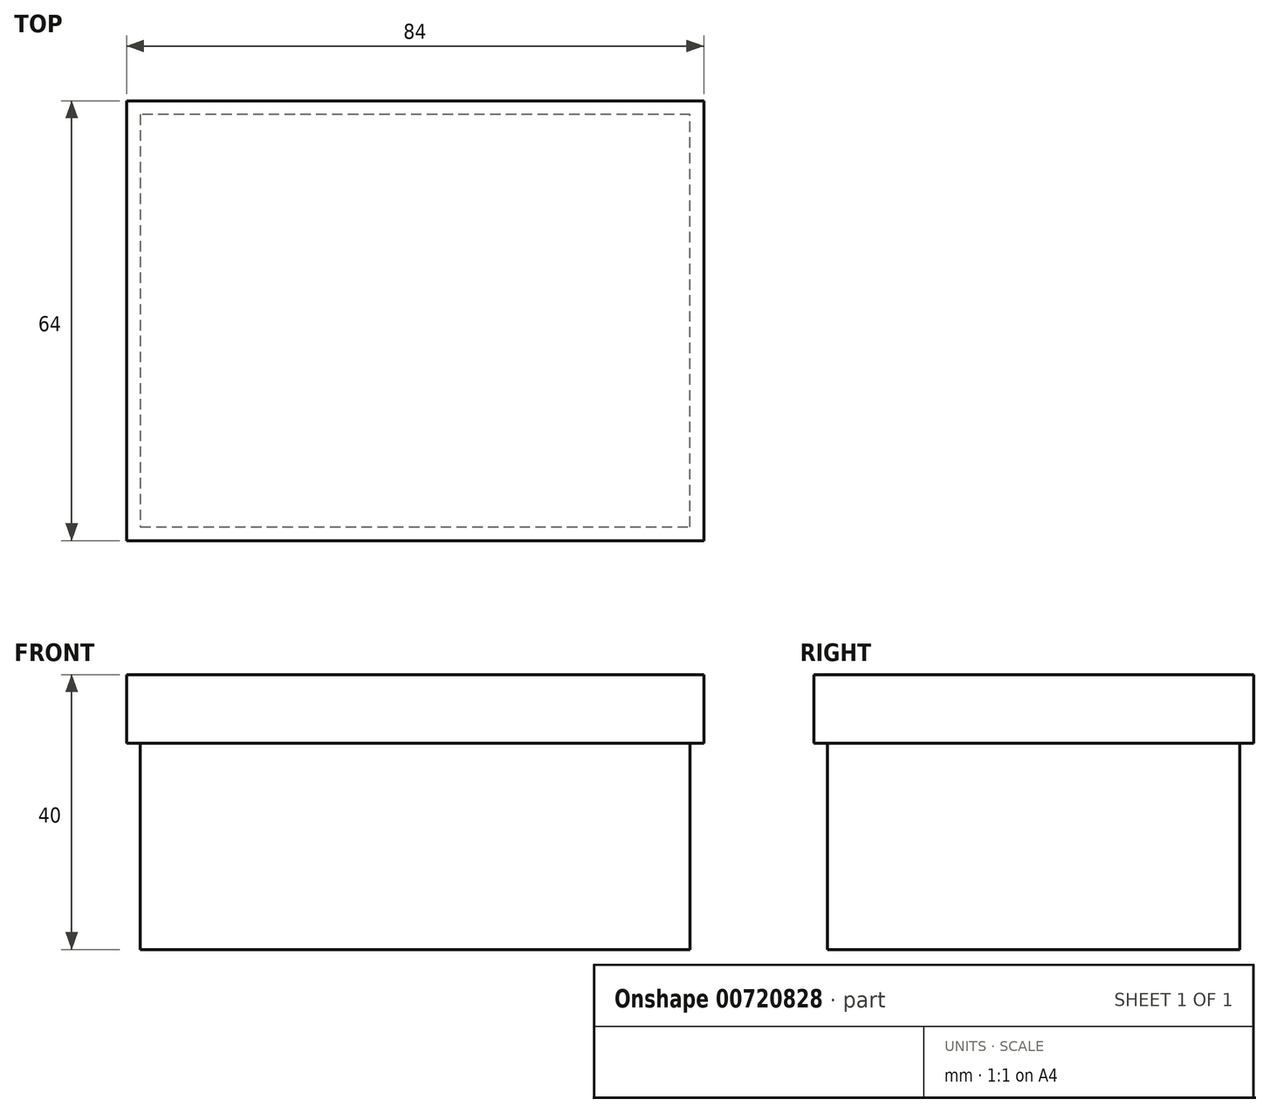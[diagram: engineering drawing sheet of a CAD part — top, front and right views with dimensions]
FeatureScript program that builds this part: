
annotation { "Feature Type Name" : "Feature", "Feature Type Description" : "" }
export const myFeature = defineFeature(function(context is Context, id is Id, definition is map)
    precondition{}
    {
        {
            var Q0;
            Q0=qCreatedBy(makeId("Top.planeOp"),FACE);
            var sketch = newSketch(context, id + "F0", { "sketchPlane" : qUnion([Q0])});
            skLineSegment(sketch, "E0.bottom", {"start": v(40, -30) * mm, "end": v(-40, -30) * mm});
            skLineSegment(sketch, "E0.top", {"start": v(40, 30) * mm, "end": v(-40, 30) * mm});
            skLineSegment(sketch, "E0.left", {"start": v(40, -30) * mm, "end": v(40, 30) * mm});
            skLineSegment(sketch, "E0.right", {"start": v(-40, -30) * mm, "end": v(-40, 30) * mm});
            skPoint(sketch, "E0.middle", {"position": v(0, 0) * mm});
            skSolve(sketch);
        }
        {
            var Q0;
            Q0=makeQuery(id+"F0.imprint","IMPRINT",FACE,{"disambiguationData":[TD([[makeQuery(id+"F0.imprint","IMPRINT",EDGE,{"derivedFrom":sQuery(id+"F0.wireOp",EDGE,"E0.bottom")}),-1.0]])]});
            extrude(context, id + "F1", {"entities" : qUnion([Q0]), "depth" : 40 * mm, "offsetDistance" : 25 * mm});
        }
        {
            var Q0;
            Q0=makeQuery(id+"F1.opExtrude","SWEPT_FACE",FACE,{"disambiguationData":[OSD([sQuery(id+"F0.wireOp",EDGE,"E0.bottom")])]});
            var sketch = newSketch(context, id + "F2", { "sketchPlane" : qUnion([Q0])});
            skLineSegment(sketch, "E1", {"start": v(-40, 40) * mm, "end": v(-40, 30) * mm});
            skLineSegment(sketch, "E2", {"start": v(-40, 30) * mm, "end": v(40, 30) * mm});
            skSolve(sketch);
        }
        {
            var Q0;
            Q0=makeQuery(id+"F2.imprint","IMPRINT",FACE,{"disambiguationData":[TD([[makeQuery(id+"F2.imprint","IMPRINT",EDGE,{"derivedFrom":sQuery(id+"F2.wireOp",EDGE,"E1")}),1.0]])]});
            extrude(context, id + "F3", {"entities" : qUnion([Q0]), "operationType" : NewBodyOperationType.ADD, "depth" : 2 * mm, "offsetDistance" : 25 * mm});
        }
        {
            var Q0;
            {var subQ0=sQuery(id+"F0.wireOp",EDGE,"E0.left");Q0=makeQuery(id+"F3.boolean.opBoolean","MERGE",FACE,{"derivedFrom":[makeQuery(id+"F1.opExtrude","SWEPT_FACE",FACE,{"disambiguationData":[OSD([subQ0])]}),makeQuery(id+"F3.opExtrude","SWEPT_FACE",FACE,{"disambiguationData":[OSD([sQuery(id+"F0.wireOp",EDGE,"E0.bottom"),subQ0])]})]});}
            var sketch = newSketch(context, id + "F4", { "sketchPlane" : qUnion([Q0])});
            skLineSegment(sketch, "E3", {"start": v(-32, 30) * mm, "end": v(30, 30) * mm});
            skSolve(sketch);
        }
        {
            var Q0;
            {var subQ0=sQuery(id+"F0.wireOp",EDGE,"E0.left");var subQ1=sQuery(id+"F0.wireOp",EDGE,"E0.bottom");var subQ3=makeQuery(id+"F3.opExtrude","CAP_EDGE",EDGE,{"disambiguationData":[OSD([subQ1,subQ0])],"isStart":false});Q0=makeQuery(id+"F4.imprint","IMPRINT",FACE,{"disambiguationData":[TD([[makeQuery(id+"F4.imprint","IMPRINT",EDGE,{"derivedFrom":subQ3}),1.0]])]});}
            extrude(context, id + "F5", {"entities" : qUnion([Q0]), "operationType" : NewBodyOperationType.ADD, "depth" : 2 * mm, "offsetDistance" : 25 * mm});
        }
        {
            var Q0;
            {var subQ0=sQuery(id+"F0.wireOp",EDGE,"E0.top");Q0=makeQuery(id+"F5.boolean.opBoolean","MERGE",FACE,{"derivedFrom":[makeQuery(id+"F1.opExtrude","SWEPT_FACE",FACE,{"disambiguationData":[OSD([subQ0])]}),makeQuery(id+"F5.opExtrude","SWEPT_FACE",FACE,{"disambiguationData":[OSD([subQ0,sQuery(id+"F0.wireOp",EDGE,"E0.left")])]})]});}
            var sketch = newSketch(context, id + "F6", { "sketchPlane" : qUnion([Q0])});
            skLineSegment(sketch, "E4", {"start": v(-42, 30) * mm, "end": v(40, 30) * mm});
            skSolve(sketch);
        }
        {
            var Q0;
            {var subQ0=sQuery(id+"F0.wireOp",EDGE,"E0.left");var subQ1=sQuery(id+"F0.wireOp",EDGE,"E0.top");var subQ3=makeQuery(id+"F5.opExtrude","CAP_EDGE",EDGE,{"disambiguationData":[OSD([subQ1,subQ0])],"isStart":false});Q0=makeQuery(id+"F6.imprint","IMPRINT",FACE,{"disambiguationData":[TD([[makeQuery(id+"F6.imprint","IMPRINT",EDGE,{"derivedFrom":subQ3}),1.0]])]});}
            extrude(context, id + "F7", {"entities" : qUnion([Q0]), "operationType" : NewBodyOperationType.ADD, "depth" : 2 * mm, "offsetDistance" : 25 * mm});
        }
        {
            var Q0;
            {var subQ0=sQuery(id+"F0.wireOp",EDGE,"E0.right");Q0=makeQuery(id+"F7.boolean.opBoolean","MERGE",FACE,{"derivedFrom":[makeQuery(id+"F3.boolean.opBoolean","MERGE",FACE,{"derivedFrom":[makeQuery(id+"F1.opExtrude","SWEPT_FACE",FACE,{"disambiguationData":[OSD([subQ0])]}),makeQuery(id+"F3.opExtrude","SWEPT_FACE",FACE,{"disambiguationData":[OSD([sQuery(id+"F2.wireOp",EDGE,"E1")])]})]}),makeQuery(id+"F7.opExtrude","SWEPT_FACE",FACE,{"disambiguationData":[OSD([sQuery(id+"F0.wireOp",EDGE,"E0.top"),subQ0])]})]});}
            var sketch = newSketch(context, id + "F8", { "sketchPlane" : qUnion([Q0])});
            skLineSegment(sketch, "E5", {"start": v(-32, 30) * mm, "end": v(32, 30) * mm});
            skSolve(sketch);
        }
        {
            var Q0;
            {var subQ0=sQuery(id+"F2.wireOp",EDGE,"E1");var subQ1=makeQuery(id+"F3.opExtrude","CAP_EDGE",EDGE,{"disambiguationData":[OSD([subQ0])],"isStart":false});Q0=makeQuery(id+"F8.imprint","IMPRINT",FACE,{"disambiguationData":[TD([[makeQuery(id+"F8.imprint","IMPRINT",EDGE,{"derivedFrom":subQ1}),-1.0]])]});}
            extrude(context, id + "F9", {"entities" : qUnion([Q0]), "operationType" : NewBodyOperationType.ADD, "depth" : 2 * mm, "offsetDistance" : 25 * mm});
        }
    });
